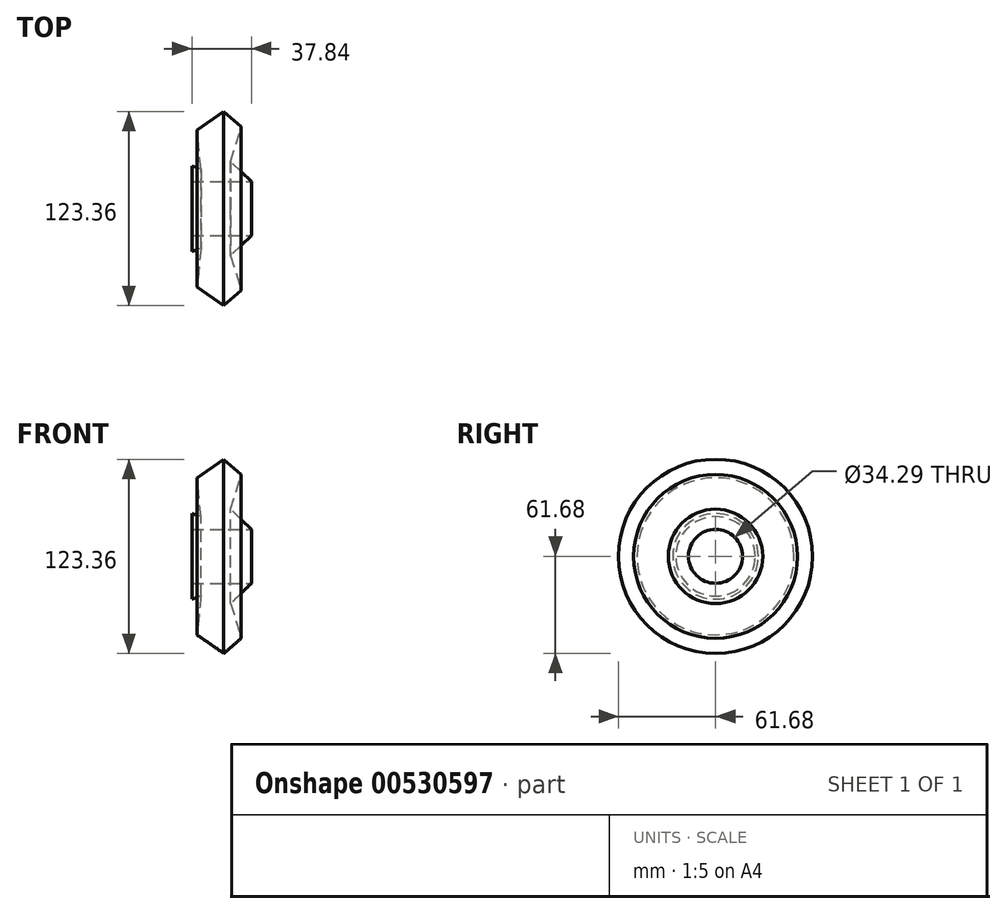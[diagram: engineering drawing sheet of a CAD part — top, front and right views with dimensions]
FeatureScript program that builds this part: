
annotation { "Feature Type Name" : "Feature", "Feature Type Description" : "" }
export const myFeature = defineFeature(function(context is Context, id is Id, definition is map)
    precondition{}
    {
        {
            var Q0;
            Q0=qCreatedBy(makeId("Front.planeOp"),FACE);
            var sketch = newSketch(context, id + "F0", { "sketchPlane" : qUnion([Q0])});
            skLineSegment(sketch, "E0", {"start": v(0, 0) * mm, "end": v(-104.45, 0) * mm});
            skLineSegment(sketch, "E1", {"start": v(0, 17.15) * mm, "end": v(-37.84, 17.15) * mm});
            skLineSegment(sketch, "E2", {"start": v(-37.84, 17.15) * mm, "end": v(-37.84, 27.2) * mm});
            skLineSegment(sketch, "E3", {"start": v(-37.84, 27.2) * mm, "end": v(-32.12, 25.22) * mm});
            skLineSegment(sketch, "E4", {"start": v(-32.12, 25.22) * mm, "end": v(-34.68, 52.03) * mm});
            skLineSegment(sketch, "E5", {"start": v(-34.48, 49.88) * mm, "end": v(-17.54, 61.68) * mm});
            skLineSegment(sketch, "E6", {"start": v(-17.54, 61.68) * mm, "end": v(-6.5, 52.03) * mm});
            skLineSegment(sketch, "E7", {"start": v(-6.5, 52.03) * mm, "end": v(-13.2, 29.95) * mm});
            skLineSegment(sketch, "E8", {"start": v(-13.2, 29.95) * mm, "end": v(0, 17.15) * mm});
            skSolve(sketch);
        }
        {
            var Q0;
            Q0=makeQuery(id+"F0.imprint","IMPRINT",FACE,{"disambiguationData":[TD([[makeQuery(id+"F0.imprint","IMPRINT",EDGE,{"derivedFrom":sQuery(id+"F0.wireOp",EDGE,"E1")}),-1.0]])]});
            var Q1;
            Q1=sQuery(id+"F0.wireOp",EDGE,"E0");
            revolve(context, id + "F1", {"entities" : qUnion([Q0]), "axis" : qUnion([Q1]), "revolveType" : RevolveType.FULL});
        }
    });
